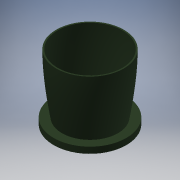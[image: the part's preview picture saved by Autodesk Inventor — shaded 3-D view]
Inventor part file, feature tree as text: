
AUTODESK INVENTOR PART (.ipt)
format: ipt  version: 2018 (Build 220112000, 112)  size: 385,024 bytes
history: native  units: in
note: dims shown in document units (in); Inventor stores cm internally (conversion verified against a paired STEP export)
features: sketch x2, revolve x2, extrude x1, pattern_circular x1
ambient origin geometry x8: Origin, YZ Plane, XZ Plane, XY Plane, X Axis, Y Axis, Z Axis, Center Point
bodies: Solid1 (feature_tree)
feature tree (6):
  sketch  "Sketch1"  dims[d0=3.5in d1=2.875in]
  revolve  "Revolution1"  [1 undecoded]
  extrude  "Extrusion2"  Depth=1.25in
  pattern_circular  "Circular Pattern2"  [2 undecoded]
  revolve  "Revolution2"  [1 undecoded]
  sketch  "Sketch3"  dims[d2=3.125in d3=1.25in d4=3.375in d6=3.625in d7=0.25in d8=3.675in d9=0.2in d10=0.75in d34=0.07in d35=0.07in d36=0.07in d37=0.07in d38=90.0deg d39=2.5in d40=0.125in d41=120.0deg d42=60.0deg d43=1.25in d44=0.125in d45=4.0in d46=0.0in d47=1.1811in d48=360.0deg d50=0.025in d51=0.025in d52=90.0deg]
note: 4 required parameter values undecoded (feature->parameter linkage not recoverable at this tier; creation-order binding heuristic only, values carry confidence <= 0.55)